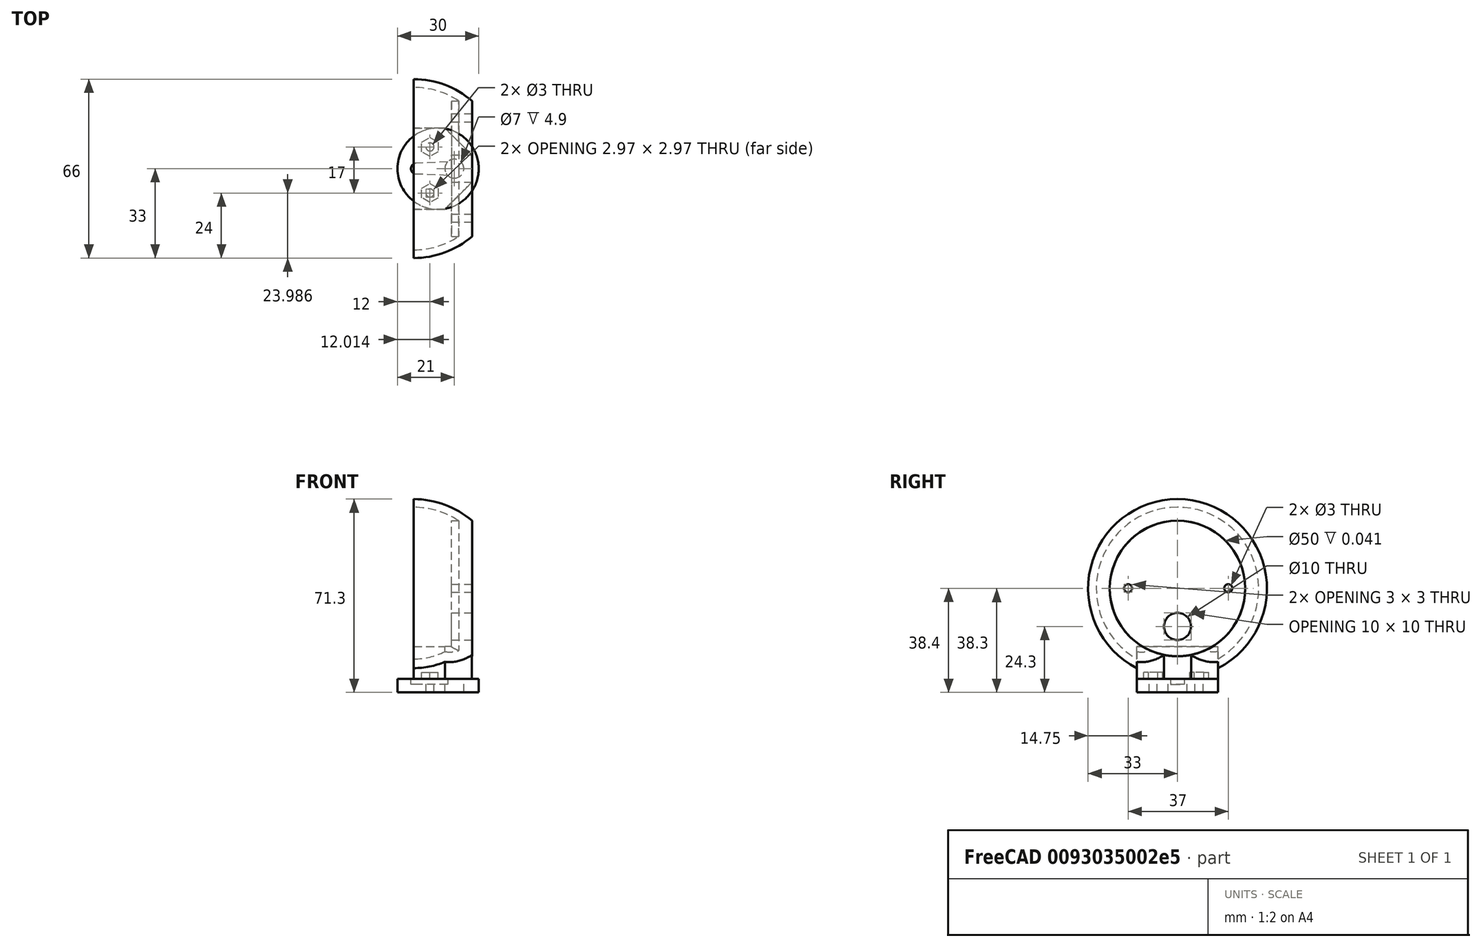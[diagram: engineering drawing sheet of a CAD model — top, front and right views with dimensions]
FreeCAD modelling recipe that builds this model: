
FCSTD DOCUMENT  (FreeCAD 0.14R3700 (Git))
Label: Radar
License: CC-BY 3.0
LicenseURL: http://creativecommons.org/licenses/by/3.0/
objects: Part::Cut×11, Part::Cylinder×10, Mesh::Feature×5, Part::MultiFuse×2, Part::Prism×2, Part::Sphere×1, Sketcher::SketchObject×1, PartDesign::Pad×1, Part::Thickness×1, Part::Box×1, Part::Chamfer×1
note: 32 computed .brp shape members not serialized (recipe doc carries the construction recipe); baked Part::Feature solids carry a one-line shape summary decoded from their .brp

FEATURE [Mesh::Feature] microServo_sg90  label="microServo-sg90"
FEATURE [Mesh::Feature] helice_1
  Placement = pos=(6,6,31.6) rot=(0,1,0;3.14159rad)
FEATURE [Mesh::Feature] moldeSensorIR
  Placement = pos=(5,21,58.6) rot=(0.57735,-0.57735,-0.57735;2.0944rad)
FEATURE [Part::Sphere] Sphere  label="Esféra"
  Angle1 = -90
  Angle2 = 90
  Angle3 = 180
  Placement = pos=(0,6,43) rot=(0,0,-1;1.5708rad)
  Radius = 30
FEATURE [Sketcher::SketchObject] Sketch
  Placement = pos=(6,6,31.6) rot=(0,1,0;3.14159rad)
  sketch-geometry (6):
    g0: Circle [constr] CenterX=0 CenterY=0 CenterZ=0 NormalX=0 NormalY=0 NormalZ=1 Radius=3.5
    g1: ArcOfCircle CenterX=14 CenterY=0 CenterZ=0 NormalX=0 NormalY=0 NormalZ=1 Radius=2 StartAngle=4.75549 EndAngle=7.81088
    g2: LineSegment StartX=2.44949 StartY=2.5 StartZ=0 EndX=2.44949 EndY=-2.5 EndZ=0
    g3: LineSegment StartX=2.44949 StartY=2.5 StartZ=0 EndX=14.0862 EndY=1.99814 EndZ=0
    g4: LineSegment StartX=2.44949 StartY=-2.5 StartZ=0 EndX=14.0862 EndY=-1.99814 EndZ=0
    g5: LineSegment [constr] StartX=14.0862 StartY=1.99814 StartZ=0 EndX=14.0862 EndY=-1.99814 EndZ=0
  constraints (17):
    c: Coincident(g0,g-1)
    c: Radius(g0) = 3.5
    c: PointOnObject(g1,g-1)
    c: Radius(g1) = 2
    c: PointOnObject(g2,g0)
    c: Vertical(g2)
    c: PointOnObject(g2,g0)
    c: DistanceY(g2) = -5
    c: Coincident(g3,g2)
    c: Tangent(g3,g1)
    c: Coincident(g4,g2)
    c: DistanceX(g-1,g1) = 14
    c: Coincident(g1,g4)
    c: Coincident(g1,g3)
    c: Coincident(g5,g1)
    c: Coincident(g5,g1)
    c: Vertical(g5)
FEATURE [PartDesign::Pad] Pad
  Length = 2
  Length2 = 100
  Placement = pos=(6,6,31.6) rot=(0,1,0;3.14159rad)
  Sketch = -> Sketch
  Type = 0
FEATURE [Part::Thickness] Thickness
  Faces = -> Sphere [Face2,Face3]
  Intersection = false
  Join = 0
  Mode = 0
  Placement = pos=(-9,0,18) rot=(0,0,1;0rad)
  SelfIntersection = false
  Value = 3
FEATURE [Part::Cylinder] Cylinder  label="Cilindro"
  Angle = 360
  Height = 4.9
  Placement = pos=(0,6,26.7) rot=(0,0,1;0rad)
  Radius = 15
FEATURE [Part::Cut] Cut
  Base = -> Cylinder
  Tool = -> Pad
FEATURE [Part::Cylinder] Cylinder001  label="Cilindro001"
  Angle = 360
  Height = 20
  Placement = pos=(6,6,22) rot=(0,0,1;0rad)
  Radius = 3.5
FEATURE [Part::Cut] Cut001
  Base = -> Cut
  Tool = -> Cylinder001
FEATURE [Part::Cylinder] Cylinder002  label="Cilindro002"
  Angle = 360
  Height = 10
  Placement = pos=(0,6,31) rot=(0,0,1;0rad)
  Radius = 1
FEATURE [Part::Cut] Cut002
  Base = -> Thickness
  Tool = -> Cylinder002
FEATURE [Part::Cylinder] Cylinder003  label="Cilindro003"
  Angle = 360
  Height = 39
  Placement = pos=(-16,24.75,61.1) rot=(0,1,0;1.5708rad)
  Radius = 1.5
FEATURE [Part::Cylinder] Cylinder004  label="Cilindro004"
  Angle = 360
  Height = 39
  Placement = pos=(-16,-12.25,61.1) rot=(0,1,0;1.5708rad)
  Radius = 1.5
FEATURE [Part::Cylinder] Cylinder005  label="Cilindro005"
  Angle = 360
  Height = 20
  Placement = pos=(5,6,61) rot=(0,1,0;1.5708rad)
  Radius = 25
FEATURE [Part::Cut] Cut003
  Base = -> Cut002
  Tool = -> Cylinder005
FEATURE [Part::Cylinder] Cylinder006  label="Cilindro006"
  Angle = 360
  Height = 7.5
  Placement = pos=(5,6,61) rot=(0,1,0;1.5708rad)
  Radius = 25
FEATURE [Part::MultiFuse] Fusion
  Shapes = -> [Cut003,Cylinder006]
FEATURE [Part::Cut] Cut004
  Base = -> Fusion
  Tool = -> Cylinder003
FEATURE [Part::Cut] Cut005
  Base = -> Cut004
  Placement = pos=(0,0,4) rot=(0,0,1;0rad)
  Tool = -> Cylinder004
FEATURE [Part::Cylinder] Cylinder007  label="Cilindro007"
  Angle = 360
  Height = 20
  Placement = pos=(0,6,51) rot=(0,1,0;1.5708rad)
  Radius = 5
FEATURE [Part::Cut] Cut006
  Base = -> Cut005
  Tool = -> Cylinder007
FEATURE [Part::Box] Box  label="Cubo"
  Height = 12
  Length = 21.5
  Placement = pos=(-9,-9,31.6) rot=(0,0,1;0rad)
  Width = 30
FEATURE [Part::Chamfer] Chamfer
  Base = -> Box
  Edges = 2 edges r=10: [Edge5,Edge7]
FEATURE [Part::MultiFuse] Fusion001
  Shapes = -> [Cut006,Chamfer]
FEATURE [Part::Prism] Prism  label="Prisma"
  Circumradius = 3.5
  Height = 3
  Placement = pos=(-3,-3,31) rot=(0,0,1;1.5708rad)
  Polygon = 6
FEATURE [Mesh::Feature] Nut_M  label="Nut-M3"
  Placement = pos=(-3,14,33) rot=(0,0,1;0rad)
FEATURE [Part::Prism] Prism001  label="Prisma001"
  Circumradius = 3.5
  Height = 3
  Placement = pos=(-3,14,31) rot=(0,0,1;1.5708rad)
  Polygon = 6
FEATURE [Part::Cut] Cut007
  Base = -> Fusion001
  Tool = -> Prism
FEATURE [Part::Cut] Cut008  label="radar"
  Base = -> Cut007
  Tool = -> Prism001
FEATURE [Part::Cylinder] Cylinder008  label="Cilindro008"
  Angle = 360
  Height = 10
  Placement = pos=(-3,-3,24) rot=(0,0,1;0rad)
  Radius = 1.5
FEATURE [Part::Cylinder] Cylinder009  label="Cilindro009"
  Angle = 360
  Height = 10
  Placement = pos=(-3,14,24) rot=(0,0,1;0rad)
  Radius = 1.5
FEATURE [Mesh::Feature] Nut_M001  label="Nut-M004"
  Placement = pos=(-3,-3,33) rot=(0,0,1;0rad)
FEATURE [Part::Cut] Cut009
  Base = -> Cut001
  Tool = -> Cylinder008
FEATURE [Part::Cut] Cut010  label="base"
  Base = -> Cut009
  Tool = -> Cylinder009
